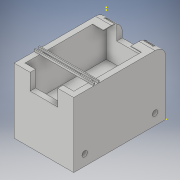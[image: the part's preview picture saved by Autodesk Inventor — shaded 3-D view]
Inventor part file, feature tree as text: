
AUTODESK INVENTOR PART (.ipt)
format: ipt  version: 2018 (Build 220112000, 112)  size: 246,272 bytes
history: native  units: mm
features: sketch x17, extrude x13, fillet x1
ambient origin geometry x8: Origin, YZ Plane, XZ Plane, XY Plane, X Axis, Y Axis, Z Axis, Center Point
bodies: Body1 (feature_tree), Body2 (feature_tree), Body3 (feature_tree)
feature tree (31):
  sketch  "Sketch10"  dims[d20=1100.0mm d21=1200.0mm]
  sketch  "Sketch11"  dims[d22=1700.0mm d23=0.0mm d24=1500.0mm]
  extrude  "Extrusion6"  Depth=1200.0mm
  extrude  "Extrusion7"  Depth=1500.0mm
  extrude  "Extrusion10"  Depth=100.0mm
  extrude  "Extrusion12"  Depth=1200.0mm TaperAngle=0.0deg
  extrude  "Extrusion13"  Depth=1500.0mm TaperAngle=0.0deg
  extrude  "Extrusion14"  Depth=10.0mm
  extrude  "Extrusion15"  Depth=1700.0mm TaperAngle=0.0deg
  extrude  "Extrusion16"  Depth=300.0mm
  sketch  "Sketch23"  dims[d63=60.0mm d64=40.0mm d65=0.0mm]
  sketch  "Sketch25"  dims[d77=100.0mm d78=80.0mm d79=600.0mm]
  extrude  "Extrusion17"  Depth=40.0mm TaperAngle=0.0deg
  extrude  "Extrusion18"  Depth=40.0mm TaperAngle=0.0deg
  extrude  "Extrusion19"  Depth=80.0mm
  sketch  "Sketch30"  dims[d86=10.0mm d87=0.0mm]
  fillet  "Fillet3"  Radius=600.0mm
  extrude  "Extrusion20"  Depth=100.0mm
  extrude  "Extrusion21"  Depth=600.0mm
  sketch  "Sketch12"  dims[d25=1000.0mm d26=0.0mm d34=100.0mm]
  sketch  "Sketch13"  dims[d35=100.0mm d36=1200.0mm d37=200.0mm d38=0.0mm d39=0.0mm]
  sketch  "Sketch16"  dims[d43=100.0mm d44=1500.0mm d45=0.0mm]
  sketch  "Sketch18"  dims[d46=900.0mm d47=10.0mm]
  sketch  "Sketch19"  dims[d48=1700.0mm d49=0.0mm d52=1700.0mm d53=0.0mm]
  sketch  "Sketch21"  dims[d58=510.0mm d59=300.0mm]
  sketch  "Sketch22"  dims[d60=100.0mm d61=40.0mm d62=0.0mm]
  sketch  "Sketch27"  dims[d81=20.0mm d82=100.0mm]
  sketch  "Sketch28"  dims[d83=80.0mm d84=600.0mm]
  sketch  "Sketch29"  dims[d85=20.0mm]
  sketch  "Sketch31"  dims[d90=250.676mm]
  sketch  "Sketch32"  dims[d91=10.0mm d92=0.0mm d93=250.676mm d94=10.0mm d95=0.0mm d96=200.0mm d97=10000.0mm d98=0.0mm d99=10000.0mm d100=0.0mm]
